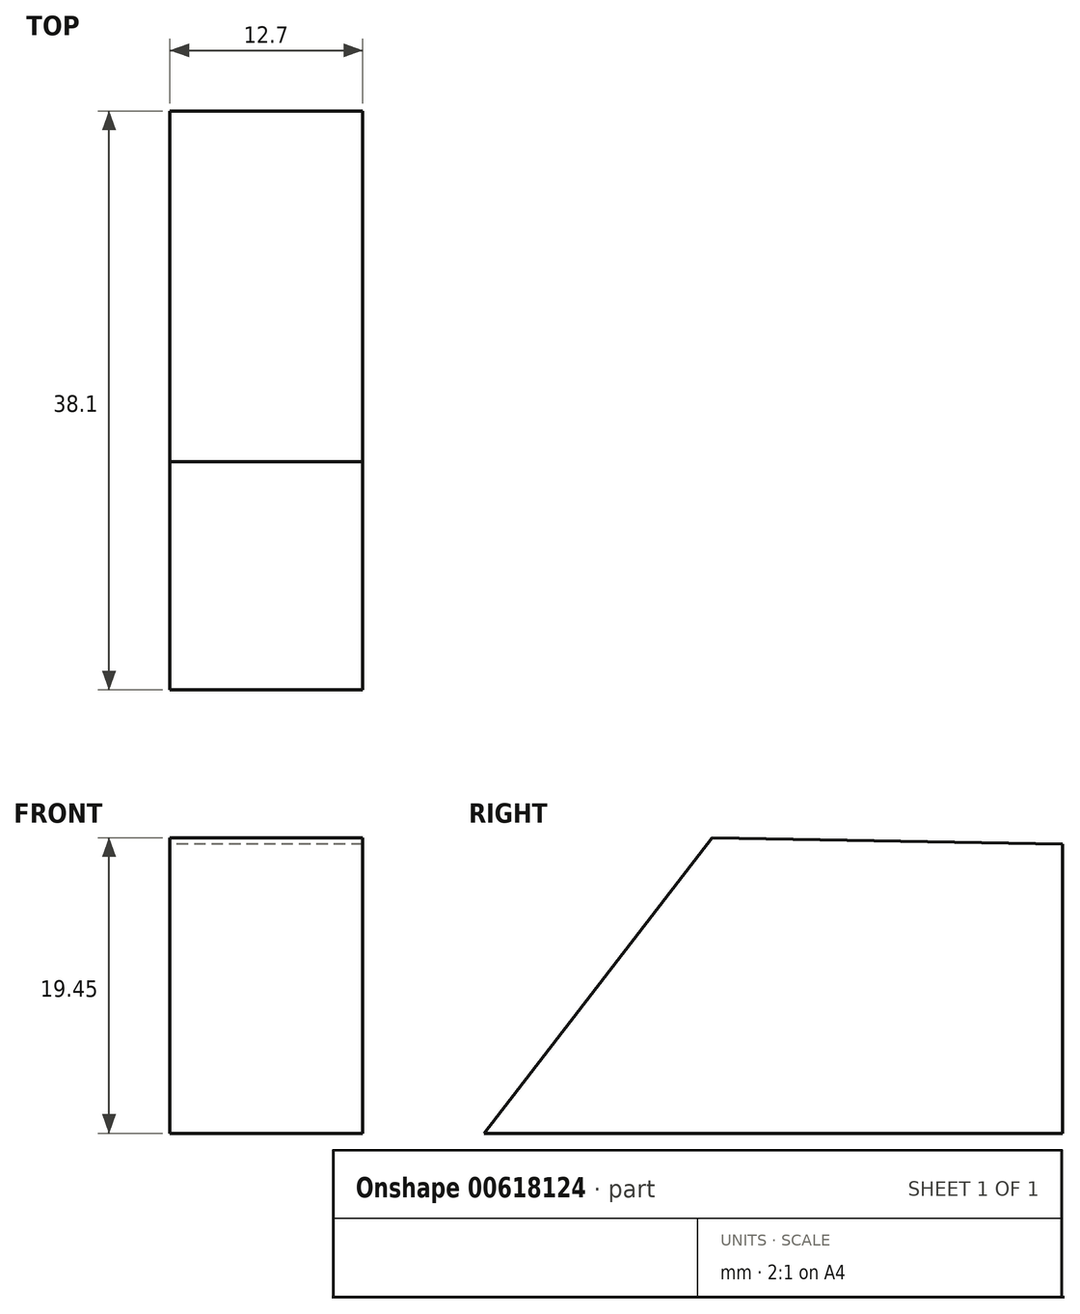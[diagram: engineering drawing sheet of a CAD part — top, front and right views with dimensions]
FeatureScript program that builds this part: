
annotation { "Feature Type Name" : "Feature", "Feature Type Description" : "" }
export const myFeature = defineFeature(function(context is Context, id is Id, definition is map)
    precondition{}
    {
        {
            var Q0;
            Q0=qCreatedBy(makeId("Right.planeOp"),FACE);
            var sketch = newSketch(context, id + "F0", { "sketchPlane" : qUnion([Q0])});
            skLineSegment(sketch, "E0", {"start": v(0, 19.05) * mm, "end": v(0, 0) * mm});
            skLineSegment(sketch, "E1", {"start": v(0, 0) * mm, "end": v(-38.1, 0) * mm});
            skLineSegment(sketch, "E2", {"start": v(-38.1, 0) * mm, "end": v(-23.1, 19.45) * mm});
            skLineSegment(sketch, "E3", {"start": v(-23.1, 19.45) * mm, "end": v(0, 19.05) * mm});
            skSolve(sketch);
        }
        {
            var Q0;
            Q0 = qSketchRegion(id + "F0", true);
            extrude(context, id + "F1", {"entities" : qUnion([Q0]), "depth" : 12.7 * mm, "offsetDistance" : 25.4 * mm});
        }
    });
